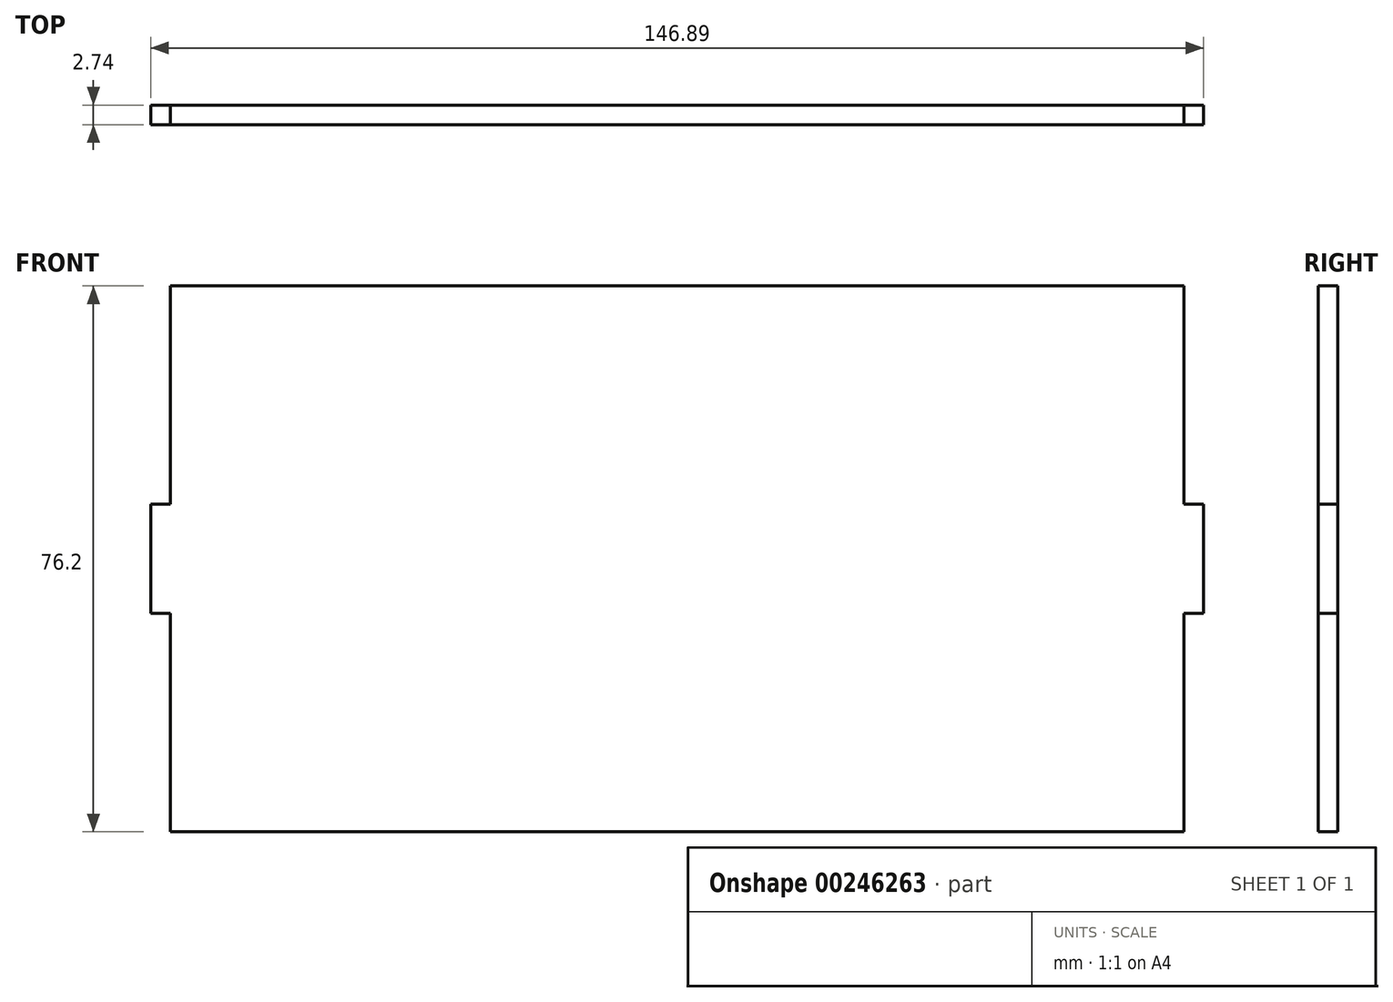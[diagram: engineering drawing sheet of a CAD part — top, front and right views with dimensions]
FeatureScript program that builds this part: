
annotation { "Feature Type Name" : "Feature", "Feature Type Description" : "" }
export const myFeature = defineFeature(function(context is Context, id is Id, definition is map)
    precondition{}
    {
        {
            var Q0;
            Q0=qCreatedBy(makeId("Front.planeOp"),FACE);
            var sketch = newSketch(context, id + "F0", { "sketchPlane" : qUnion([Q0])});
            skLineSegment(sketch, "E0.bottom", {"start": v(-87.2, 30.48) * mm, "end": v(54.2, 30.48) * mm});
            skLineSegment(sketch, "E0.top", {"start": v(-87.2, -45.72) * mm, "end": v(54.2, -45.72) * mm});
            skLineSegment(sketch, "E0.left", {"start": v(-87.2, 30.48) * mm, "end": v(-87.2, -45.72) * mm});
            skLineSegment(sketch, "E0.right", {"start": v(54.2, 30.48) * mm, "end": v(54.2, -45.72) * mm});
            skLineSegment(sketch, "E1", {"start": v(-16.5, 30.48) * mm, "end": v(-16.5, -45.72) * mm, "construction": true});
            skLineSegment(sketch, "E2", {"start": v(-87.2, -7.62) * mm, "end": v(54.2, -7.62) * mm, "construction": true});
            skLineSegment(sketch, "E3", {"start": v(-24.11, 27.73) * mm, "end": v(-24.11, 30.48) * mm});
            skLineSegment(sketch, "E4.MirrorCS", {"start": v(-8.87, 27.73) * mm, "end": v(-8.87, 30.48) * mm});
            skLineSegment(sketch, "E5", {"start": v(-24.11, 27.73) * mm, "end": v(-8.87, 27.73) * mm});
            skLineSegment(sketch, "E6.MirrorCS", {"start": v(-24.11, -42.98) * mm, "end": v(-8.87, -42.98) * mm});
            skLineSegment(sketch, "E7.MirrorCS", {"start": v(-8.87, -42.98) * mm, "end": v(-8.87, -45.72) * mm});
            skLineSegment(sketch, "E8.MirrorCS", {"start": v(-24.11, -42.98) * mm, "end": v(-24.11, -45.72) * mm});
            skLineSegment(sketch, "E9.MirrorCS", {"start": v(-89.94, 0) * mm, "end": v(-87.2, 0) * mm});
            skLineSegment(sketch, "E10.MirrorCS", {"start": v(-89.94, -15.24) * mm, "end": v(-87.2, -15.24) * mm});
            skLineSegment(sketch, "E11.MirrorCS", {"start": v(-89.94, 0) * mm, "end": v(-89.94, -15.24) * mm});
            skLineSegment(sketch, "E12.MirrorCS", {"start": v(56.95, 0) * mm, "end": v(56.95, -15.24) * mm});
            skLineSegment(sketch, "E13.MirrorCS", {"start": v(56.95, 0) * mm, "end": v(54.2, 0) * mm});
            skLineSegment(sketch, "E14.MirrorCS", {"start": v(56.95, -15.24) * mm, "end": v(54.2, -15.24) * mm});
            skSolve(sketch);
        }
        {
            var Q0;
            {var subQ10=sQuery(id+"F0.wireOp",EDGE,"E3");Q0=makeQuery(id+"F0.imprint","IMPRINT",FACE,{"disambiguationData":[TD([[makeQuery(id+"F0.imprint","IMPRINT",EDGE,{"derivedFrom":subQ10}),1.0]])]});}
            var Q1;
            Q1=makeQuery(id+"F0.imprint","IMPRINT",FACE,{"disambiguationData":[TD([[makeQuery(id+"F0.imprint","IMPRINT",EDGE,{"derivedFrom":sQuery(id+"F0.wireOp",EDGE,"2a6bfd6c-9bbf-46f3-97a7-c3288baa15e50.MirrorCS")}),-1.0]])]});
            var Q2;
            {var subQ0=sQuery(id+"F0.wireOp",EDGE,"E9.MirrorCS");Q2=makeQuery(id+"F0.imprint","IMPRINT",FACE,{"disambiguationData":[TD([[makeQuery(id+"F0.imprint","IMPRINT",EDGE,{"derivedFrom":subQ0}),-1.0]])]});}
            var Q3;
            Q3=makeQuery(id+"F0.imprint","IMPRINT",FACE,{"disambiguationData":[TD([[makeQuery(id+"F0.imprint","IMPRINT",EDGE,{"derivedFrom":sQuery(id+"F0.wireOp",EDGE,"E12.MirrorCS")}),-1.0]])]});
            var Q4;
            {var subQ0=sQuery(id+"F0.wireOp",EDGE,"E3");Q4=makeQuery(id+"F0.imprint","IMPRINT",FACE,{"disambiguationData":[TD([[makeQuery(id+"F0.imprint","IMPRINT",EDGE,{"derivedFrom":subQ0}),-1.0]])]});}
            var Q5;
            Q5=makeQuery(id+"F0.imprint","IMPRINT",FACE,{"disambiguationData":[TD([[makeQuery(id+"F0.imprint","IMPRINT",EDGE,{"derivedFrom":sQuery(id+"F0.wireOp",EDGE,"E6.MirrorCS")}),-1.0]])]});
            extrude(context, id + "F1", {"entities" : qUnion([Q0, Q1, Q2, Q3, Q4, Q5]), "depth" : 2.74 * mm});
        }
    });
